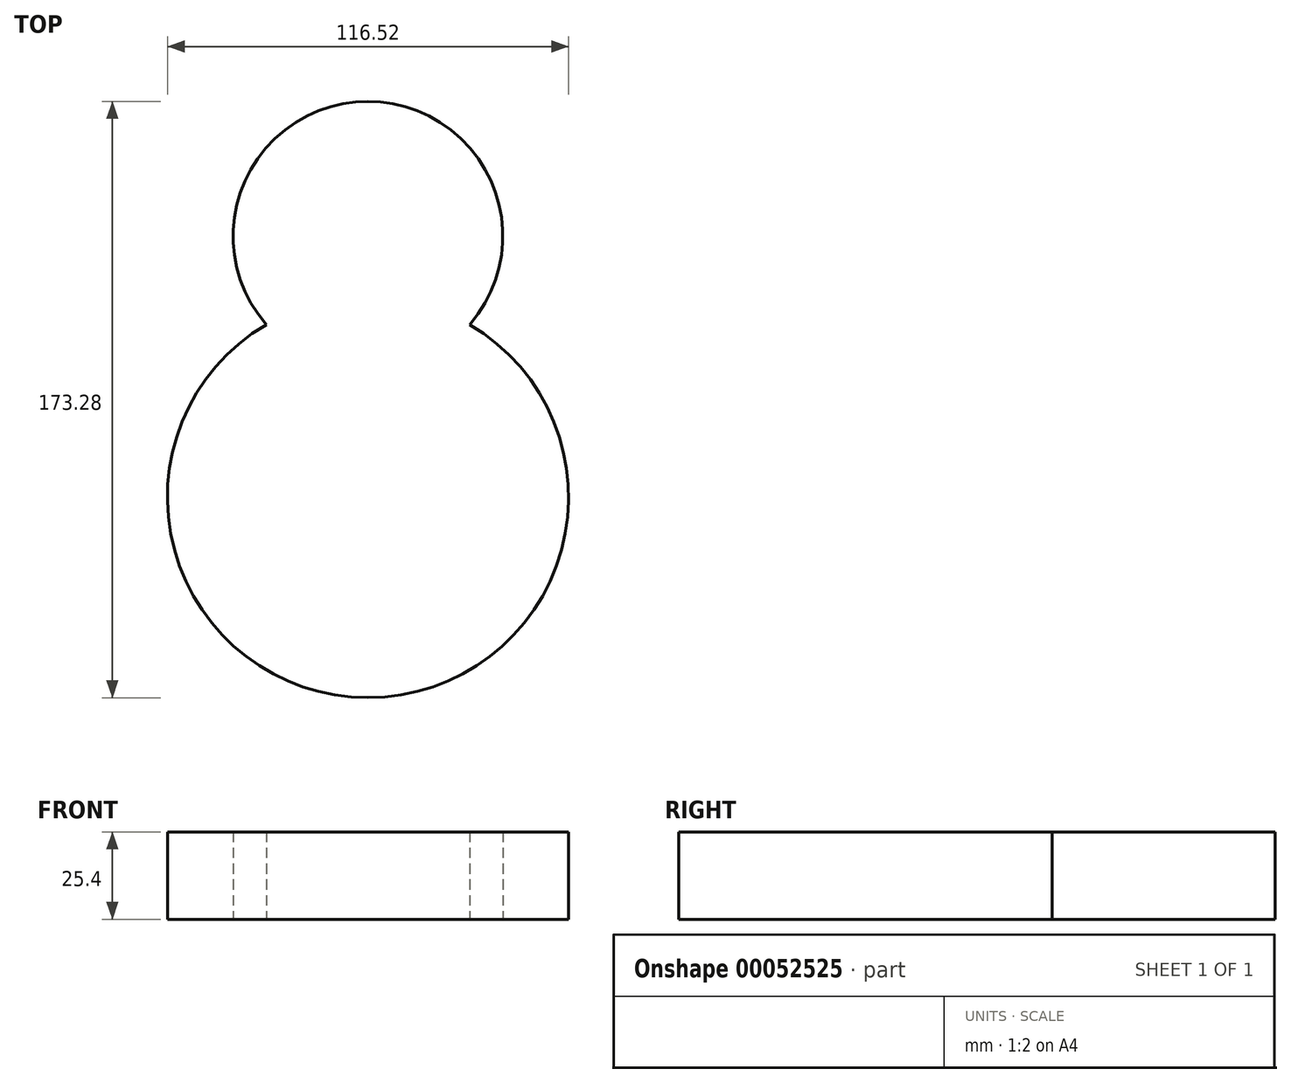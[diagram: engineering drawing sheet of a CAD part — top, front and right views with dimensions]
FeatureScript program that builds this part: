
annotation { "Feature Type Name" : "Feature", "Feature Type Description" : "" }
export const myFeature = defineFeature(function(context is Context, id is Id, definition is map)
    precondition{}
    {
        {
            var Q0;
            Q0=qCreatedBy(makeId("Top.planeOp"),FACE);
            var sketch = newSketch(context, id + "F0", { "sketchPlane" : qUnion([Q0])});
            skCircle(sketch, "E0", {"center": v(0, 0) * mm, "radius": 58.26 * mm});
            skCircle(sketch, "E1", {"center": v(0, 75.87) * mm, "radius": 39.15 * mm});
            skSolve(sketch);
        }
        {
            var Q0;
            Q0 = qSketchRegion(id + "F0", true);
            extrude(context, id + "F1", {"entities" : qUnion([Q0]), "depth" : 25.4 * mm});
        }
    });
